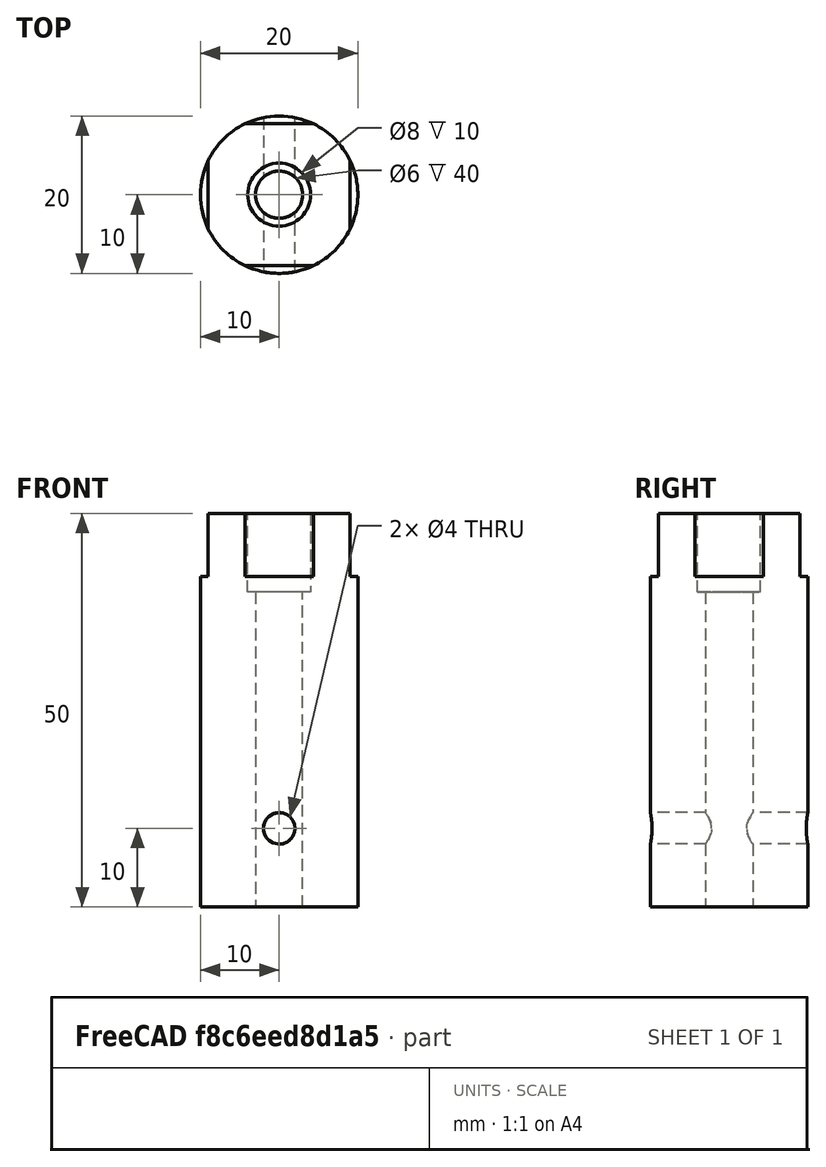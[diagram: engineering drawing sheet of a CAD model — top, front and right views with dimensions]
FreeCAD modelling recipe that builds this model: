
FCSTD DOCUMENT  (FreeCAD 0.20R)
Label: JECCbot_mini_wheeladapter_18mm
License: All rights reserved
LicenseURL: http://en.wikipedia.org/wiki/All_rights_reserved
objects: TechDraw::DrawViewDimension×11, Sketcher::SketchObject×5, PartDesign::Pocket×4, TechDraw::DrawViewPart×4, TechDraw::DrawViewAnnotation×4, PartDesign::Pad×1, PartDesign::Body×1, TechDraw::DrawSVGTemplate×1, TechDraw::DrawPage×1
note: 16 computed .brp shape members not serialized (recipe doc carries the construction recipe); baked Part::Feature solids carry a one-line shape summary decoded from their .brp

FEATURE [Sketcher::SketchObject] Sketch061
  FullyConstrained = false
  MapMode = 5
  Support = -> [XY_Plane026]
  sketch-geometry (2):
    g0: Circle CenterX=0 CenterY=0 CenterZ=0 NormalX=0 NormalY=0 NormalZ=1 AngleXU=0 Radius=10
    g1: Circle CenterX=0 CenterY=0 CenterZ=0 NormalX=0 NormalY=0 NormalZ=1 AngleXU=0 Radius=0
  constraints (4):
    c: Coincident(g0,g-1)
    c: Diameter(g0) = 20
    c: Coincident(g1,g0)
    c: Tangent(g1,g-1)
FEATURE [PartDesign::Pad] Pad011
  AllowMultiFace = false
  Direction = (1,1,1)
  Length = 50
  Length2 = 100
  Profile = -> Sketch061
  Type = 0
FEATURE [Sketcher::SketchObject] Sketch062
  FullyConstrained = false
  MapMode = 5
  Placement = pos=(0,0,0) rot=(1,0,0;3.14159rad)
  Support = -> [Pad011]
  sketch-geometry (1):
    g0: Circle CenterX=0 CenterY=0 CenterZ=0 NormalX=0 NormalY=0 NormalZ=1 AngleXU=0 Radius=3
  constraints (2):
    c: Coincident(g0,g-1)
    c: Diameter(g0) = 6
FEATURE [PartDesign::Pocket] Pocket052
  AllowMultiFace = false
  BaseFeature = -> Pad011
  Direction = (1,1,1)
  Length = 5
  Length2 = 100
  Profile = -> Sketch062
  Type = 1
FEATURE [Sketcher::SketchObject] Sketch063
  FullyConstrained = false
  MapMode = 5
  Placement = pos=(0,0,50) rot=(0,0,1;0rad)
  Support = -> [Pocket052]
  sketch-geometry (8):
    g0: LineSegment StartX=-9 StartY=-9 StartZ=0 EndX=9 EndY=-9 EndZ=0
    g1: LineSegment StartX=9 StartY=-9 StartZ=0 EndX=9 EndY=9 EndZ=0
    g2: LineSegment StartX=9 StartY=9 StartZ=0 EndX=-9 EndY=9 EndZ=0
    g3: LineSegment StartX=-9 StartY=9 StartZ=0 EndX=-9 EndY=-9 EndZ=0
    g4: LineSegment StartX=-15 StartY=15 StartZ=0 EndX=15 EndY=15 EndZ=0
    g5: LineSegment StartX=15 StartY=15 StartZ=0 EndX=15 EndY=-15 EndZ=0
    g6: LineSegment StartX=15 StartY=-15 StartZ=0 EndX=-15 EndY=-15 EndZ=0
    g7: LineSegment StartX=-15 StartY=-15 StartZ=0 EndX=-15 EndY=15 EndZ=0
  constraints (18):
    c: Coincident(g0,g1)
    c: Coincident(g1,g2)
    c: Coincident(g2,g3)
    c: Coincident(g3,g0)
    c: Symmetric(g1,g0,g-1)
    c: Symmetric(g2,g0,g-1)
    c: Symmetric(g2,g1,g-2)
    c: DistanceX(g2,g1) = 18
    c: DistanceY(g0,g1) = 18
    c: Coincident(g4,g5)
    c: Coincident(g5,g6)
    c: Coincident(g6,g7)
    c: Coincident(g7,g4)
    c: Symmetric(g4,g6,g-1)
    c: Symmetric(g4,g5,g-1)
    c: Symmetric(g4,g4,g-2)
    c: DistanceX(g4,g4) = 30
    c: DistanceY(g5,g4) = 30
FEATURE [PartDesign::Pocket] Pocket053
  AllowMultiFace = false
  BaseFeature = -> Pocket052
  Direction = (1,1,1)
  Length = 8
  Length2 = 100
  Profile = -> Sketch063
  Type = 0
FEATURE [Sketcher::SketchObject] Sketch064
  FullyConstrained = false
  MapMode = 5
  Placement = pos=(0,0,50) rot=(0,0,1;0rad)
  Support = -> [Pocket053]
  sketch-geometry (1):
    g0: Circle CenterX=0 CenterY=0 CenterZ=0 NormalX=0 NormalY=0 NormalZ=1 AngleXU=0 Radius=4
  constraints (2):
    c: Coincident(g0,g-1)
    c: Diameter(g0) = 8
FEATURE [PartDesign::Pocket] Pocket054
  AllowMultiFace = false
  BaseFeature = -> Pocket053
  Direction = (1,1,1)
  Length = 10
  Length2 = 100
  Profile = -> Sketch064
  Type = 0
FEATURE [Sketcher::SketchObject] Sketch065
  FullyConstrained = false
  MapMode = 5
  Placement = pos=(0,0,0) rot=(1,0,0;1.5708rad)
  Support = -> [XZ_Plane026]
  sketch-geometry (1):
    g0: Circle CenterX=0 CenterY=10 CenterZ=0 NormalX=0 NormalY=0 NormalZ=1 AngleXU=0 Radius=2
  constraints (3):
    c: PointOnObject(g0,g-2)
    c: DistanceY(g-1,g0) = 10
    c: Diameter(g0) = 4
FEATURE [PartDesign::Pocket] Pocket055
  AllowMultiFace = false
  BaseFeature = -> Pocket054
  Direction = (1,1,1)
  Length = 5
  Length2 = 100
  Midplane = true
  Profile = -> Sketch065
  Type = 1
FEATURE [PartDesign::Body] Body011  label="wheeldadapter_18mm"
  Group = -> [Sketch061,Pad011,Sketch062,Pocket052,Sketch063,Pocket053,Sketch064,Pocket054,Sketch065,Pocket055]
  Origin = -> Origin026
  Tip = -> Pocket055
FEATURE [TechDraw::DrawSVGTemplate] Template
  EditableTexts = Designed_by_Name=Bernhard Mayer; Drawing_number=Drawing number; FC-Date=2020-01-11; FC-SC=1:1; FC-SH=Sheet; FC-Title=JECCbot mini; Subtitle=Wheel adapter 18mm; Weight=Weight
  Height = 210
  Orientation = 1
  Width = 297
FEATURE [TechDraw::DrawViewPart] View
  CoarseView = false
  Direction = (0,0,1)
  Focus = 100
  HardHidden = false
  IsoCount = 0
  IsoHidden = false
  IsoVisible = false
  LockPosition = false
  Perspective = false
  Rotation = 0
  ScaleType = 0
  SeamHidden = false
  SeamVisible = false
  SmoothHidden = false
  SmoothVisible = false
  Source = -> [Body011]
  X = 100
  XDirection = (1,0,0)
  Y = 40
FEATURE [TechDraw::DrawViewPart] View001
  CoarseView = false
  Direction = (1,0,0)
  Focus = 100
  HardHidden = true
  IsoCount = 0
  IsoHidden = false
  IsoVisible = false
  LockPosition = false
  Perspective = false
  Rotation = 0
  ScaleType = 0
  SeamHidden = false
  SeamVisible = false
  SmoothHidden = false
  SmoothVisible = false
  Source = -> [Body011]
  X = 100
  XDirection = (0,1,0)
  Y = 130
FEATURE [TechDraw::DrawViewPart] View002
  CoarseView = false
  Direction = (0,1,0)
  Focus = 100
  HardHidden = false
  IsoCount = 0
  IsoHidden = false
  IsoVisible = false
  LockPosition = false
  Perspective = false
  Rotation = 0
  ScaleType = 0
  SeamHidden = false
  SeamVisible = false
  SmoothHidden = false
  SmoothVisible = false
  Source = -> [Body011]
  X = 50
  XDirection = (-1,0,0)
  Y = 130
FEATURE [TechDraw::DrawViewPart] View003
  CoarseView = false
  Direction = (1,1,1)
  Focus = 100
  HardHidden = false
  IsoCount = 0
  IsoHidden = false
  IsoVisible = false
  LockPosition = false
  Perspective = false
  Rotation = 45
  ScaleType = 0
  SeamHidden = false
  SeamVisible = false
  SmoothHidden = false
  SmoothVisible = false
  Source = -> [Body011]
  X = 214.5
  XDirection = (-0.707107,0.707107,0)
  Y = 105
FEATURE [TechDraw::DrawViewDimension] Dimension
  AngleOverride = false
  Arbitrary = false
  ArbitraryTolerances = false
  EqualTolerance = false
  ExtensionAngle = 0
  FormatSpec = %.2f
  FormatSpecOverTolerance = %+.2w
  FormatSpecUnderTolerance = %+.2w
  Inverted = false
  LineAngle = 0
  LockPosition = false
  MeasureType = 1
  OverTolerance = 0
  References2D = -> [View001]
  Rotation = 0
  ScaleType = 0
  TheoreticalExact = false
  Type = 1
  UnderTolerance = 0
  X = 1.04949
  Y = -40.5934
FEATURE [TechDraw::DrawViewDimension] Dimension001
  AngleOverride = false
  Arbitrary = false
  ArbitraryTolerances = false
  EqualTolerance = false
  ExtensionAngle = 0
  FormatSpec = %.2f
  FormatSpecOverTolerance = %+.2w
  FormatSpecUnderTolerance = %+.2w
  Inverted = false
  LineAngle = 0
  LockPosition = false
  MeasureType = 1
  OverTolerance = 0
  References2D = -> [View001]
  Rotation = 0
  ScaleType = 0
  TheoreticalExact = false
  Type = 1
  UnderTolerance = 0
  X = -1.90685
  Y = 46.6829
FEATURE [TechDraw::DrawViewDimension] Dimension002
  AngleOverride = false
  Arbitrary = false
  ArbitraryTolerances = false
  EqualTolerance = false
  ExtensionAngle = 0
  FormatSpec = %.2f
  FormatSpecOverTolerance = %+.2w
  FormatSpecUnderTolerance = %+.2w
  Inverted = false
  LineAngle = 0
  LockPosition = false
  MeasureType = 1
  OverTolerance = 0
  References2D = -> [View001]
  Rotation = 0
  ScaleType = 0
  TheoreticalExact = false
  Type = 2
  UnderTolerance = 0
  X = 21.3006
  Y = 34.7399
FEATURE [TechDraw::DrawViewDimension] Dimension003
  AngleOverride = false
  Arbitrary = false
  ArbitraryTolerances = false
  EqualTolerance = false
  ExtensionAngle = 0
  FormatSpec = %.2f
  FormatSpecOverTolerance = %+.2w
  FormatSpecUnderTolerance = %+.2w
  Inverted = false
  LineAngle = 0
  LockPosition = false
  MeasureType = 1
  OverTolerance = 0
  References2D = -> [View001]
  Rotation = 0
  ScaleType = 0
  TheoreticalExact = false
  Type = 2
  UnderTolerance = 0
  X = 34.208
  Y = 1.04191
FEATURE [TechDraw::DrawViewDimension] Dimension004
  AngleOverride = false
  Arbitrary = false
  ArbitraryTolerances = false
  EqualTolerance = false
  ExtensionAngle = 0
  FormatSpec = %.2f
  FormatSpecOverTolerance = %+.2w
  FormatSpecUnderTolerance = %+.2w
  Inverted = false
  LineAngle = 0
  LockPosition = false
  MeasureType = 1
  OverTolerance = 0
  References2D = -> [View002]
  Rotation = 0
  ScaleType = 0
  TheoreticalExact = false
  Type = 2
  UnderTolerance = 0
  X = 17.9494
  Y = -21.4884
FEATURE [TechDraw::DrawViewDimension] Dimension005
  AngleOverride = false
  Arbitrary = false
  ArbitraryTolerances = false
  EqualTolerance = false
  ExtensionAngle = 0
  FormatSpec = ⌀%.2f
  FormatSpecOverTolerance = %+.2w
  FormatSpecUnderTolerance = %+.2w
  Inverted = false
  LineAngle = 0
  LockPosition = false
  MeasureType = 1
  OverTolerance = 0
  References2D = -> [View]
  Rotation = 0
  ScaleType = 0
  TheoreticalExact = false
  Type = 5
  UnderTolerance = 0
  X = -2.23954
  Y = -20.0698
FEATURE [TechDraw::DrawViewDimension] Dimension006
  AngleOverride = false
  Arbitrary = false
  ArbitraryTolerances = false
  EqualTolerance = false
  ExtensionAngle = 0
  FormatSpec = ⌀%.2f
  FormatSpecOverTolerance = %+.2w
  FormatSpecUnderTolerance = %+.2w
  Inverted = false
  LineAngle = 0
  LockPosition = false
  MeasureType = 1
  OverTolerance = 0
  References2D = -> [View]
  Rotation = 0
  ScaleType = 0
  TheoreticalExact = false
  Type = 5
  UnderTolerance = 0
  X = -0.68909
  Y = 16.3659
FEATURE [TechDraw::DrawViewAnnotation] Annotation
  Font = osifont
  LineSpace = 80
  LockPosition = false
  MaxWidth = -1
  Rotation = 0
  ScaleType = 0
  Text = M8
  TextSize = 3
  TextStyle = 0
  X = 90.4132
  Y = 16.0631
FEATURE [TechDraw::DrawViewAnnotation] Annotation001
  Font = osifont
  LineSpace = 80
  LockPosition = false
  MaxWidth = -1
  Rotation = 0
  ScaleType = 0
  Text = M4
  TextSize = 3
  TextStyle = 0
  X = 53.9903
  Y = 120.742
FEATURE [TechDraw::DrawViewDimension] Dimension007
  AngleOverride = false
  Arbitrary = false
  ArbitraryTolerances = false
  EqualTolerance = false
  ExtensionAngle = 0
  FormatSpec = %.2f
  FormatSpecOverTolerance = %+.2w
  FormatSpecUnderTolerance = %+.2w
  Inverted = false
  LineAngle = 0
  LockPosition = false
  MeasureType = 1
  OverTolerance = 0
  References2D = -> [View001]
  Rotation = 0
  ScaleType = 0
  TheoreticalExact = false
  Type = 2
  UnderTolerance = 0
  X = 28.0311
  Y = 35.2738
FEATURE [TechDraw::DrawViewDimension] Dimension008
  AngleOverride = false
  Arbitrary = false
  ArbitraryTolerances = false
  EqualTolerance = false
  ExtensionAngle = 0
  FormatSpec = %.2f
  FormatSpecOverTolerance = %+.2w
  FormatSpecUnderTolerance = %+.2w
  Inverted = false
  LineAngle = 0
  LockPosition = false
  MeasureType = 1
  OverTolerance = 0
  References2D = -> [View001]
  Rotation = 0
  ScaleType = 0
  TheoreticalExact = false
  Type = 1
  UnderTolerance = 0
  X = 0.393157
  Y = 37.0954
FEATURE [TechDraw::DrawViewDimension] Dimension009
  AngleOverride = false
  Arbitrary = false
  ArbitraryTolerances = false
  EqualTolerance = false
  ExtensionAngle = 0
  FormatSpec = %.2f
  FormatSpecOverTolerance = %+.2w
  FormatSpecUnderTolerance = %+.2w
  Inverted = false
  LineAngle = 0
  LockPosition = false
  MeasureType = 1
  OverTolerance = 0
  References2D = -> [View001]
  Rotation = 0
  ScaleType = 0
  TheoreticalExact = false
  Type = 1
  UnderTolerance = 0
  X = 1.33959
  Y = -32.182
FEATURE [TechDraw::DrawViewDimension] Dimension010
  AngleOverride = false
  Arbitrary = false
  ArbitraryTolerances = false
  EqualTolerance = false
  ExtensionAngle = 0
  FormatSpec = %.2f
  FormatSpecOverTolerance = %+.2w
  FormatSpecUnderTolerance = %+.2w
  Inverted = false
  LineAngle = 0
  LockPosition = false
  MeasureType = 1
  OverTolerance = 0
  References2D = -> [View001]
  Rotation = 0
  ScaleType = 0
  TheoreticalExact = false
  Type = 2
  UnderTolerance = 0
  X = 16.6397
  Y = -3.81424
FEATURE [TechDraw::DrawViewAnnotation] Annotation002
  Font = osifont
  LineSpace = 80
  LockPosition = false
  MaxWidth = -1
  Rotation = 0
  ScaleType = 0
  Text = M4
  TextSize = 3
  TextStyle = 0
  X = 119.28
  Y = 115.996
FEATURE [TechDraw::DrawViewAnnotation] Annotation003
  Font = osifont
  LineSpace = 80
  LockPosition = false
  MaxWidth = -1
  Rotation = 0
  ScaleType = 0
  Text = M8
  TextSize = 3
  TextStyle = 0
  X = 99.8981
  Y = 162.994
FEATURE [TechDraw::DrawPage] Page  label="wheeladapter 18mm"
  KeepUpdated = true
  NextBalloonIndex = 1
  ProjectionType = 0
  Template = -> Template
  Views = -> [View,View001,View002,View003,Dimension,Dimension001,Dimension002,Dimension003,Dimension004,Dimension005,Dimension006,Annotation,Annotation001,Dimension007,Dimension008,Dimension009,Dimension010,Annotation002,Annotation003]
